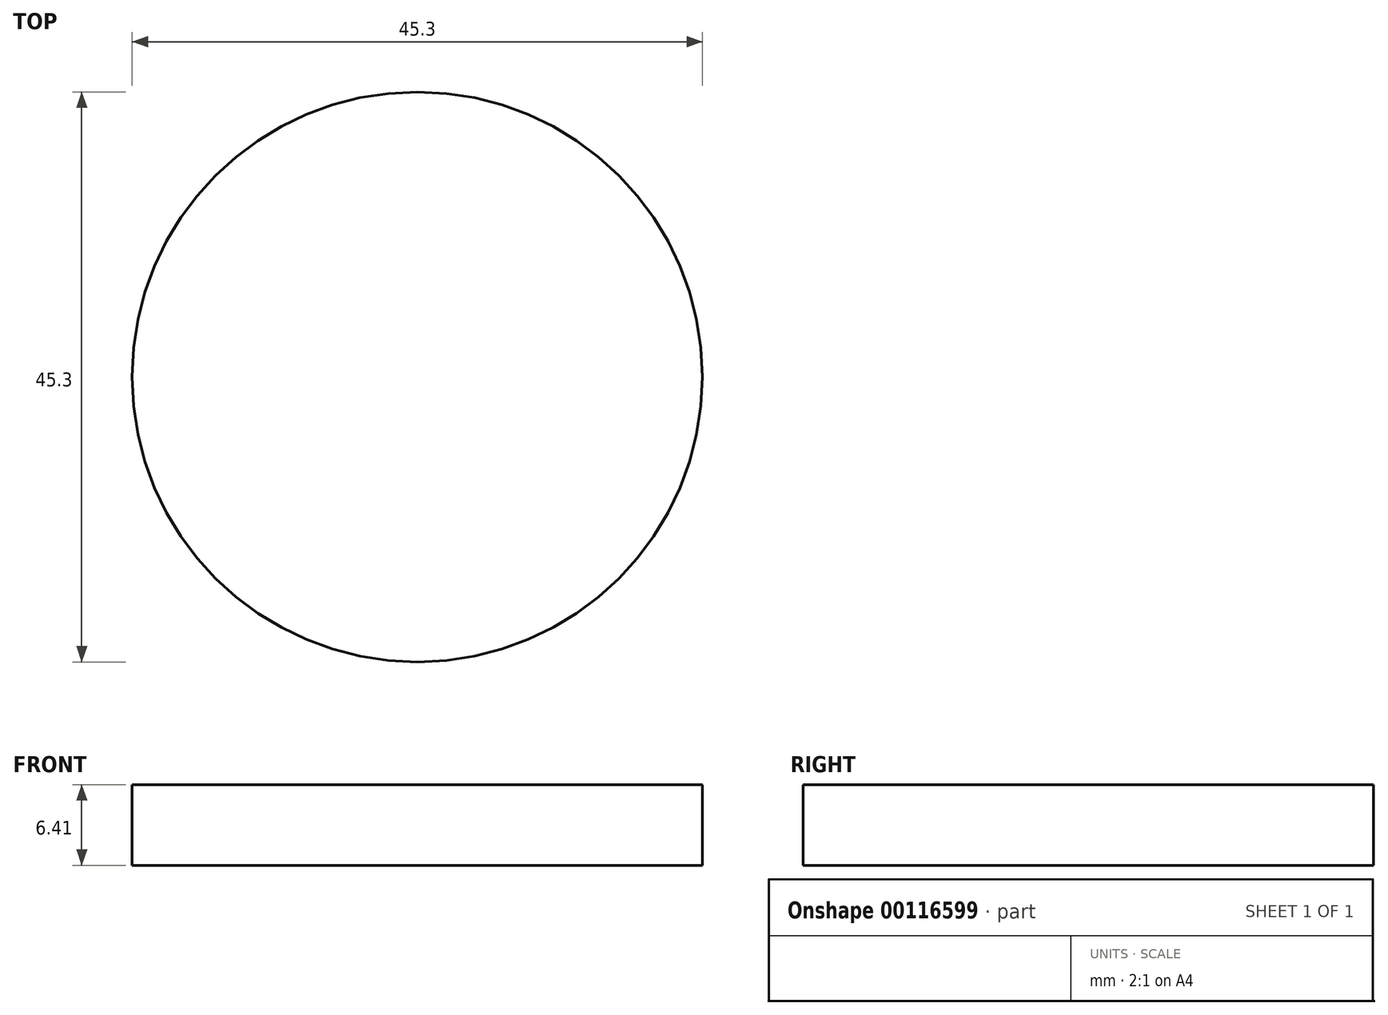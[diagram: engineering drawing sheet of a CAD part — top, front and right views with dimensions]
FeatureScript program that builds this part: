
annotation { "Feature Type Name" : "Feature", "Feature Type Description" : "" }
export const myFeature = defineFeature(function(context is Context, id is Id, definition is map)
    precondition{}
    {
        {
            var Q0;
            Q0=qCreatedBy(makeId("Front.planeOp"),FACE);
            var sketch = newSketch(context, id + "F0", { "sketchPlane" : qUnion([Q0])});
            skLineSegment(sketch, "E0.bottom", {"start": v(0, 0) * mm, "end": v(22.65, 0) * mm});
            skLineSegment(sketch, "E0.top", {"start": v(0, 6.4) * mm, "end": v(22.65, 6.4) * mm});
            skLineSegment(sketch, "E0.left", {"start": v(0, 0) * mm, "end": v(0, 6.4) * mm});
            skLineSegment(sketch, "E0.right", {"start": v(22.65, 0) * mm, "end": v(22.65, 6.4) * mm});
            skLineSegment(sketch, "E1.bottom", {"start": v(0, 0) * mm, "end": v(7.6, 0) * mm});
            skLineSegment(sketch, "E1.top", {"start": v(0, -67.35) * mm, "end": v(7.6, -67.35) * mm});
            skLineSegment(sketch, "E1.left", {"start": v(0, 0) * mm, "end": v(0, -67.35) * mm});
            skLineSegment(sketch, "E1.right", {"start": v(7.6, 0) * mm, "end": v(7.6, -67.35) * mm});
            skLineSegment(sketch, "E2", {"start": v(7.6, -67.35) * mm, "end": v(0, -76.88) * mm});
            skLineSegment(sketch, "E3", {"start": v(0, -67.35) * mm, "end": v(0, -76.88) * mm});
            skSolve(sketch);
        }
        {
            var Q0;
            Q0=makeQuery(id+"F0.imprint","IMPRINT",FACE,{"disambiguationData":[TD([[makeQuery(id+"F0.imprint","IMPRINT",EDGE,{"derivedFrom":sQuery(id+"F0.wireOp",EDGE,"E0.bottom")}),1.0]])]});
            var Q1;
            Q1=sQuery(id+"F0.wireOp",EDGE,"E0.left");
            revolve(context, id + "F1", {"entities" : qUnion([Q0]), "axis" : qUnion([Q1]), "revolveType" : RevolveType.ONE_DIRECTION, "angle" : 360 * degree});
        }
    });
